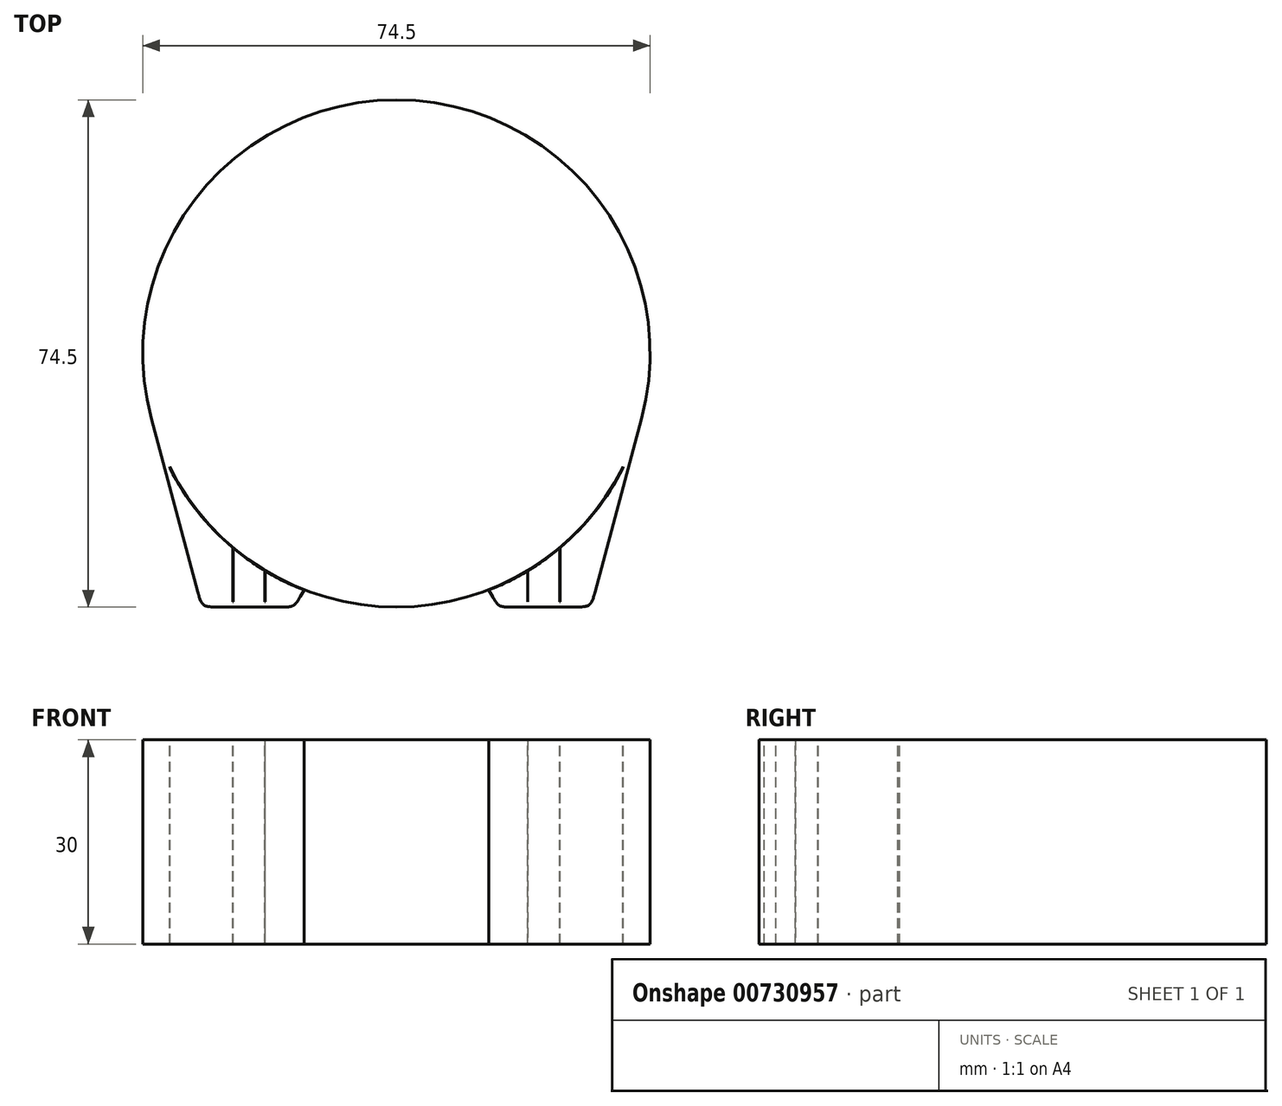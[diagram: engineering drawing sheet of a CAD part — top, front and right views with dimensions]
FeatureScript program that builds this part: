
annotation { "Feature Type Name" : "Feature", "Feature Type Description" : "" }
export const myFeature = defineFeature(function(context is Context, id is Id, definition is map)
    precondition{}
    {
        {
            var Q0;
            Q0=qCreatedBy(makeId("Top.planeOp"),FACE);
            var sketch = newSketch(context, id + "F0", { "sketchPlane" : qUnion([Q0])});
            skCircle(sketch, "E0", {"center": v(0, 0) * mm, "radius": 36.75 * mm});
            skSolve(sketch);
        }
        {
            var Q0;
            Q0=qCreatedBy(makeId("Top.planeOp"),FACE);
            var sketch = newSketch(context, id + "F1", { "sketchPlane" : qUnion([Q0])});
            skArc(sketch, "E1", {"start": v(35.98, -9.64) * mm, "mid": v(29.55, 22.68) * mm, "end": v(0, 37.25) * mm});
            skLineSegment(sketch, "E2", {"start": v(35.98, -9.64) * mm, "end": v(28.58, -37.25) * mm});
            skLineSegment(sketch, "E3", {"start": v(28.58, -37.25) * mm, "end": v(15, -37.25) * mm});
            skLineSegment(sketch, "E4", {"start": v(13.53, -34.7) * mm, "end": v(15, -37.25) * mm});
            skLineSegment(sketch, "E5", {"start": v(-30.16, -36.75) * mm, "end": v(38.04, -36.75) * mm, "construction": true});
            skLineSegment(sketch, "E6", {"start": v(0, 37.25) * mm, "end": v(0, -37.25) * mm});
            skArc(sketch, "E7", {"start": v(0, -37.25) * mm, "mid": v(6.88, -36.6) * mm, "end": v(13.53, -34.7) * mm});
            skSolve(sketch);
        }
        {
            var Q0;
            Q0=makeQuery(id+"F1.imprint","IMPRINT",FACE,{"disambiguationData":[TD([[makeQuery(id+"F1.imprint","IMPRINT",EDGE,{"derivedFrom":sQuery(id+"F1.wireOp",EDGE,"E1")}),1.0]])]});
            extrude(context, id + "F2", {"entities" : qUnion([Q0]), "depth" : 30 * mm, "offsetDistance" : 25 * mm});
        }
        {
            var Q0;
            Q0=makeQuery(id+"F2.opExtrude","CAP_FACE",FACE,{"disambiguationData":[OSD([sQuery(id+"F1.wireOp",EDGE,"E1"),sQuery(id+"F1.wireOp",EDGE,"E2"),sQuery(id+"F1.wireOp",EDGE,"E3"),sQuery(id+"F1.wireOp",EDGE,"E4"),sQuery(id+"F1.wireOp",EDGE,"E6"),sQuery(id+"F1.wireOp",EDGE,"E7")])],"isStart":false});
            var sketch = newSketch(context, id + "F3", { "sketchPlane" : qUnion([Q0])});
            skArc(sketch, "E8", {"start": v(13.53, -34.7) * mm, "mid": v(25.11, -27.51) * mm, "end": v(33.33, -16.63) * mm});
            skArc(sketch, "E9", {"start": v(13.56, -34.75) * mm, "mid": v(25.06, -27.63) * mm, "end": v(33.27, -16.87) * mm});
            skLineSegment(sketch, "E10", {"start": v(13.56, -34.75) * mm, "end": v(13.53, -34.7) * mm});
            skLineSegment(sketch, "E11", {"start": v(33.27, -16.87) * mm, "end": v(33.33, -16.63) * mm});
            skSolve(sketch);
        }
        {
            var Q0;
            Q0 = qSketchRegion(id + "F3", true);
            extrude(context, id + "F4", {"entities" : qUnion([Q0]), "operationType" : NewBodyOperationType.REMOVE, "endBound" : BoundingType.THROUGH_ALL, "oppositeDirection" : true, "depth" : 25 * mm, "offsetDistance" : 25 * mm});
        }
        {
            var Q0;
            Q0=makeQuery(id+"F2.opExtrude","SWEPT_EDGE",EDGE,{"disambiguationData":[OSD([sQuery(id+"F1.wireOp",EDGE,"E3"),sQuery(id+"F1.wireOp",EDGE,"E4")])]});
            var Q1;
            Q1=makeQuery(id+"F2.opExtrude","SWEPT_EDGE",EDGE,{"disambiguationData":[OSD([sQuery(id+"F1.wireOp",EDGE,"E2"),sQuery(id+"F1.wireOp",EDGE,"E3")])]});
            fillet(context, id + "F5", {"entities" : qUnion([Q0, Q1]), "radius" : 3 * mm, "tangentPropagation" : true, "rho" : .7, "crossSection" : FilletCrossSection.CONIC, "allowEdgeOverflow" : false});
        }
        {
            var Q0;
            Q0=makeQuery(id+"F2.opExtrude","CAP_FACE",FACE,{"disambiguationData":[OSD([sQuery(id+"F1.wireOp",EDGE,"E1"),sQuery(id+"F1.wireOp",EDGE,"E2"),sQuery(id+"F1.wireOp",EDGE,"E3"),sQuery(id+"F1.wireOp",EDGE,"E4"),sQuery(id+"F1.wireOp",EDGE,"E6"),sQuery(id+"F1.wireOp",EDGE,"E7")])],"isStart":false});
            var sketch = newSketch(context, id + "F6", { "sketchPlane" : qUnion([Q0])});
            skLineSegment(sketch, "E12", {"start": v(19.26, -31.94) * mm, "end": v(19.26, -36.5) * mm});
            skLineSegment(sketch, "E13", {"start": v(19.26, -36.5) * mm, "end": v(19.3, -36.5) * mm});
            skLineSegment(sketch, "E14", {"start": v(19.3, -36.5) * mm, "end": v(19.3, -31.91) * mm});
            skLineSegment(sketch, "E15", {"start": v(19.3, -31.91) * mm, "end": v(19.26, -31.94) * mm});
            skLineSegment(sketch, "E16", {"start": v(23.96, -28.59) * mm, "end": v(23.96, -36.5) * mm});
            skLineSegment(sketch, "E17", {"start": v(23.96, -36.5) * mm, "end": v(24, -36.5) * mm});
            skLineSegment(sketch, "E18", {"start": v(24, -36.5) * mm, "end": v(24, -28.48) * mm});
            skLineSegment(sketch, "E19", {"start": v(24, -28.48) * mm, "end": v(23.96, -28.59) * mm});
            skLineSegment(sketch, "E20", {"start": v(19.3, -36.5) * mm, "end": v(23.96, -36.5) * mm, "construction": true});
            skLineSegment(sketch, "E21", {"start": v(24, -36.5) * mm, "end": v(28.66, -36.5) * mm, "construction": true});
            skLineSegment(sketch, "E22", {"start": v(19.26, -36.5) * mm, "end": v(14.6, -36.5) * mm, "construction": true});
            skSolve(sketch);
        }
        {
            var Q0;
            Q0 = qSketchRegion(id + "F6", true);
            extrude(context, id + "F7", {"entities" : qUnion([Q0]), "operationType" : NewBodyOperationType.REMOVE, "endBound" : BoundingType.THROUGH_ALL, "oppositeDirection" : true, "depth" : 25 * mm, "offsetDistance" : 25 * mm});
        }
        {
            var Q0;
            Q0=makeQuery(id+"F2.opExtrude","SWEPT_BODY",BODY,{"disambiguationData":[OSD([sQuery(id+"F1.wireOp",EDGE,"E1"),sQuery(id+"F1.wireOp",EDGE,"E2"),sQuery(id+"F1.wireOp",EDGE,"E3"),sQuery(id+"F1.wireOp",EDGE,"E4"),sQuery(id+"F1.wireOp",EDGE,"E6"),sQuery(id+"F1.wireOp",EDGE,"E7")])]});
            var Q1;
            Q1=makeQuery(id+"F2.opExtrude","SWEPT_FACE",FACE,{"disambiguationData":[OSD([sQuery(id+"F1.wireOp",EDGE,"E6")])]});
            mirror(context, id + "F8", {"operationType" : NewBodyOperationType.ADD, "entities" : qUnion([Q0]), "mirrorPlane" : qUnion([Q1])});
        }
    });
